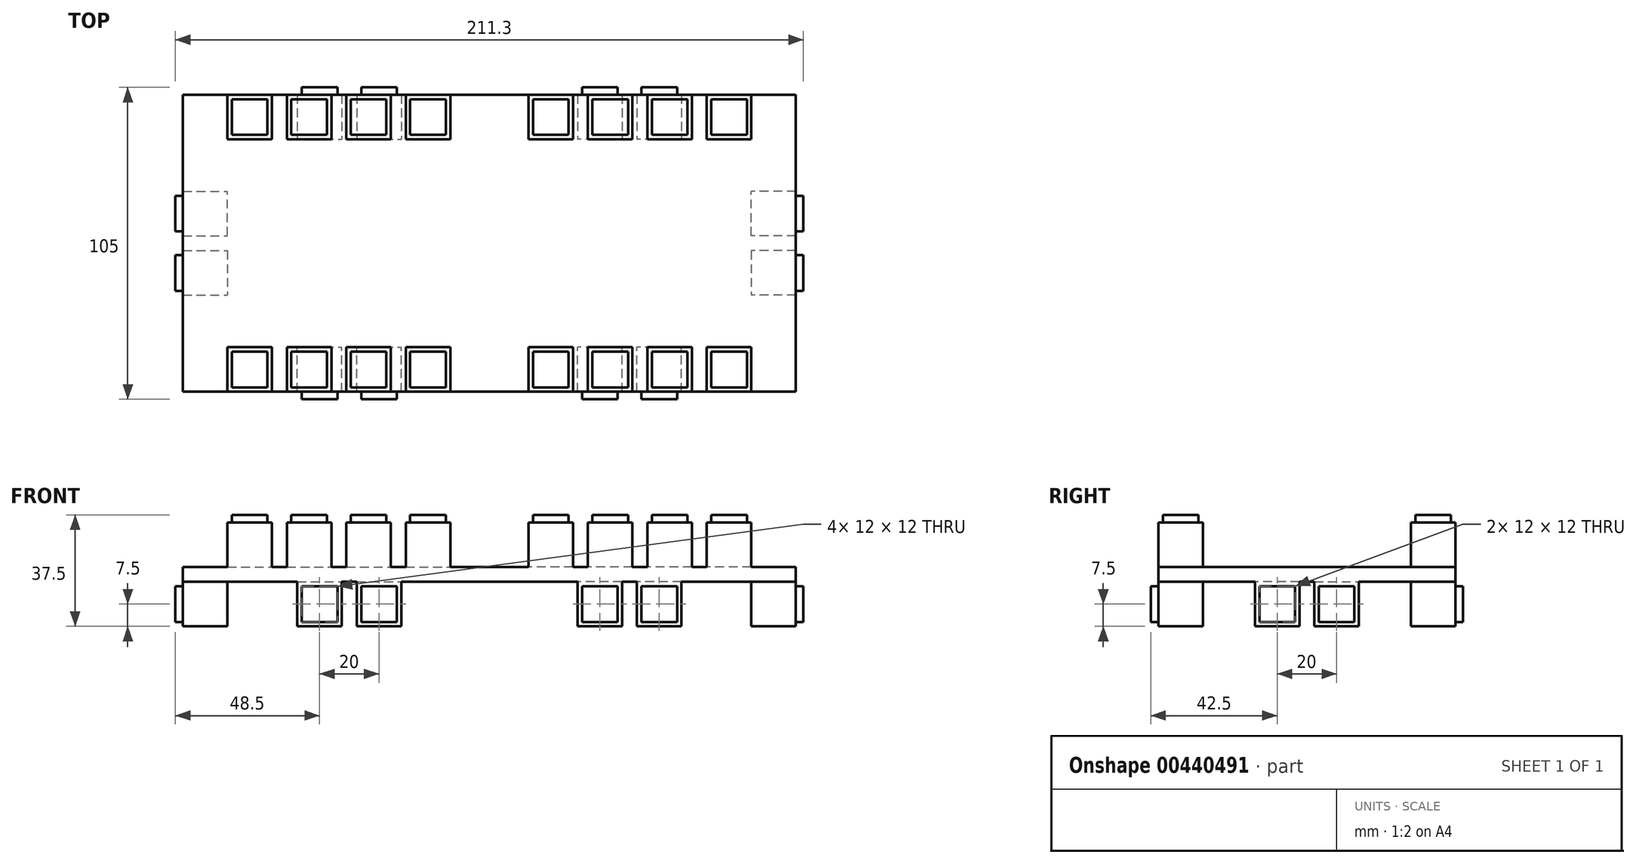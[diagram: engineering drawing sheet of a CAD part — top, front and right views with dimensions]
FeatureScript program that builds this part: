
annotation { "Feature Type Name" : "Feature", "Feature Type Description" : "" }
export const myFeature = defineFeature(function(context is Context, id is Id, definition is map)
    precondition{}
    {
        {
            var Q0;
            Q0=qCreatedBy(makeId("Top.planeOp"),FACE);
            var sketch = newSketch(context, id + "F0", { "sketchPlane" : qUnion([Q0])});
            skLineSegment(sketch, "E0.bottom", {"start": v(-103.15, 50) * mm, "end": v(103.15, 50) * mm});
            skLineSegment(sketch, "E0.top", {"start": v(-103.15, -50) * mm, "end": v(103.15, -50) * mm});
            skLineSegment(sketch, "E0.left", {"start": v(-103.15, 50) * mm, "end": v(-103.15, -50) * mm});
            skLineSegment(sketch, "E0.right", {"start": v(103.15, 50) * mm, "end": v(103.15, -50) * mm});
            skPoint(sketch, "E0.middle", {"position": v(0, 0) * mm});
            skSolve(sketch);
        }
        {
            var Q0;
            Q0 = qSketchRegion(id + "F0", true);
            extrude(context, id + "F1", {"entities" : qUnion([Q0]), "depth" : 5 * mm});
        }
        {
            var Q0;
            Q0=makeQuery(id+"F1.opExtrude","CAP_FACE",FACE,{"disambiguationData":[OSD([sQuery(id+"F0.wireOp",EDGE,"E0.bottom"),sQuery(id+"F0.wireOp",EDGE,"E0.top"),sQuery(id+"F0.wireOp",EDGE,"E0.left"),sQuery(id+"F0.wireOp",EDGE,"E0.right")])],"isStart":false});
            var sketch = newSketch(context, id + "F2", { "sketchPlane" : qUnion([Q0])});
            skLineSegment(sketch, "E1.bottom", {"start": v(-88.15, 50) * mm, "end": v(-73.15, 50) * mm});
            skLineSegment(sketch, "E1.top", {"start": v(-88.15, 35) * mm, "end": v(-73.15, 35) * mm});
            skLineSegment(sketch, "E1.left", {"start": v(-88.15, 50) * mm, "end": v(-88.15, 35) * mm});
            skLineSegment(sketch, "E1.right", {"start": v(-73.15, 50) * mm, "end": v(-73.15, 35) * mm});
            skLineSegment(sketch, "E2.bottom", {"start": v(-68.15, 50) * mm, "end": v(-53.15, 50) * mm});
            skLineSegment(sketch, "E2.top", {"start": v(-68.15, 35) * mm, "end": v(-53.15, 35) * mm});
            skLineSegment(sketch, "E2.left", {"start": v(-68.15, 50) * mm, "end": v(-68.15, 35) * mm});
            skLineSegment(sketch, "E2.right", {"start": v(-53.15, 50) * mm, "end": v(-53.15, 35) * mm});
            skLineSegment(sketch, "E3.bottom", {"start": v(-48.15, 50) * mm, "end": v(-33.15, 50) * mm});
            skLineSegment(sketch, "E3.top", {"start": v(-48.15, 35) * mm, "end": v(-33.15, 35) * mm});
            skLineSegment(sketch, "E3.left", {"start": v(-48.15, 50) * mm, "end": v(-48.15, 35) * mm});
            skLineSegment(sketch, "E3.right", {"start": v(-33.15, 50) * mm, "end": v(-33.15, 35) * mm});
            skLineSegment(sketch, "E4.bottom", {"start": v(-28.15, 50) * mm, "end": v(-13.15, 50) * mm});
            skLineSegment(sketch, "E4.top", {"start": v(-28.15, 35) * mm, "end": v(-13.15, 35) * mm});
            skLineSegment(sketch, "E4.left", {"start": v(-28.15, 50) * mm, "end": v(-28.15, 35) * mm});
            skLineSegment(sketch, "E4.right", {"start": v(-13.15, 50) * mm, "end": v(-13.15, 35) * mm});
            skLineSegment(sketch, "E5", {"start": v(0, 50) * mm, "end": v(0, -50) * mm, "construction": true});
            skLineSegment(sketch, "E6", {"start": v(-103.15, 0) * mm, "end": v(103.15, 0) * mm, "construction": true});
            skLineSegment(sketch, "E7.MirrorCS", {"start": v(-28.15, -35) * mm, "end": v(-13.15, -35) * mm});
            skLineSegment(sketch, "E8.MirrorCS", {"start": v(-13.15, -50) * mm, "end": v(-13.15, -35) * mm});
            skLineSegment(sketch, "E9.MirrorCS", {"start": v(-28.15, -50) * mm, "end": v(-13.15, -50) * mm});
            skLineSegment(sketch, "E10.MirrorCS", {"start": v(-28.15, -50) * mm, "end": v(-28.15, -35) * mm});
            skLineSegment(sketch, "E11.MirrorCS", {"start": v(-48.15, -35) * mm, "end": v(-33.15, -35) * mm});
            skLineSegment(sketch, "E12.MirrorCS", {"start": v(-33.15, -50) * mm, "end": v(-33.15, -35) * mm});
            skLineSegment(sketch, "E13.MirrorCS", {"start": v(-48.15, -50) * mm, "end": v(-33.15, -50) * mm});
            skLineSegment(sketch, "E14.MirrorCS", {"start": v(-48.15, -50) * mm, "end": v(-48.15, -35) * mm});
            skLineSegment(sketch, "E15.MirrorCS", {"start": v(-68.15, -35) * mm, "end": v(-53.15, -35) * mm});
            skLineSegment(sketch, "E16.MirrorCS", {"start": v(-53.15, -50) * mm, "end": v(-53.15, -35) * mm});
            skLineSegment(sketch, "E17.MirrorCS", {"start": v(-68.15, -50) * mm, "end": v(-53.15, -50) * mm});
            skLineSegment(sketch, "E18.MirrorCS", {"start": v(-68.15, -50) * mm, "end": v(-68.15, -35) * mm});
            skLineSegment(sketch, "E19.MirrorCS", {"start": v(-73.15, -50) * mm, "end": v(-73.15, -35) * mm});
            skLineSegment(sketch, "E20.MirrorCS", {"start": v(-88.15, -35) * mm, "end": v(-73.15, -35) * mm});
            skLineSegment(sketch, "E21.MirrorCS", {"start": v(-88.15, -50) * mm, "end": v(-73.15, -50) * mm});
            skLineSegment(sketch, "E22.MirrorCS", {"start": v(-88.15, -50) * mm, "end": v(-88.15, -35) * mm});
            skLineSegment(sketch, "E23.MirrorCS", {"start": v(28.15, -50) * mm, "end": v(13.15, -50) * mm});
            skLineSegment(sketch, "E24.MirrorCS", {"start": v(13.15, -50) * mm, "end": v(13.15, -35) * mm});
            skLineSegment(sketch, "E25.MirrorCS", {"start": v(28.15, -35) * mm, "end": v(13.15, -35) * mm});
            skLineSegment(sketch, "E26.MirrorCS", {"start": v(28.15, -50) * mm, "end": v(28.15, -35) * mm});
            skLineSegment(sketch, "E27.MirrorCS", {"start": v(48.15, -50) * mm, "end": v(33.15, -50) * mm});
            skLineSegment(sketch, "E28.MirrorCS", {"start": v(33.15, -50) * mm, "end": v(33.15, -35) * mm});
            skLineSegment(sketch, "E29.MirrorCS", {"start": v(48.15, -35) * mm, "end": v(33.15, -35) * mm});
            skLineSegment(sketch, "E30.MirrorCS", {"start": v(48.15, -50) * mm, "end": v(48.15, -35) * mm});
            skLineSegment(sketch, "E31.MirrorCS", {"start": v(53.15, -50) * mm, "end": v(53.15, -35) * mm});
            skLineSegment(sketch, "E32.MirrorCS", {"start": v(68.15, -50) * mm, "end": v(53.15, -50) * mm});
            skLineSegment(sketch, "E33.MirrorCS", {"start": v(68.15, -50) * mm, "end": v(68.15, -35) * mm});
            skLineSegment(sketch, "E34.MirrorCS", {"start": v(68.15, -35) * mm, "end": v(53.15, -35) * mm});
            skLineSegment(sketch, "E35.MirrorCS", {"start": v(88.15, -50) * mm, "end": v(73.15, -50) * mm});
            skLineSegment(sketch, "E36.MirrorCS", {"start": v(73.15, -50) * mm, "end": v(73.15, -35) * mm});
            skLineSegment(sketch, "E37.MirrorCS", {"start": v(88.15, -35) * mm, "end": v(73.15, -35) * mm});
            skLineSegment(sketch, "E38.MirrorCS", {"start": v(88.15, -50) * mm, "end": v(88.15, -35) * mm});
            skLineSegment(sketch, "E39.MirrorCS", {"start": v(28.15, 35) * mm, "end": v(13.15, 35) * mm});
            skLineSegment(sketch, "E40.MirrorCS", {"start": v(13.15, 50) * mm, "end": v(13.15, 35) * mm});
            skLineSegment(sketch, "E41.MirrorCS", {"start": v(28.15, 50) * mm, "end": v(13.15, 50) * mm});
            skLineSegment(sketch, "E42.MirrorCS", {"start": v(28.15, 50) * mm, "end": v(28.15, 35) * mm});
            skLineSegment(sketch, "E43.MirrorCS", {"start": v(48.15, 35) * mm, "end": v(33.15, 35) * mm});
            skLineSegment(sketch, "E44.MirrorCS", {"start": v(33.15, 50) * mm, "end": v(33.15, 35) * mm});
            skLineSegment(sketch, "E45.MirrorCS", {"start": v(48.15, 50) * mm, "end": v(33.15, 50) * mm});
            skLineSegment(sketch, "E46.MirrorCS", {"start": v(48.15, 50) * mm, "end": v(48.15, 35) * mm});
            skLineSegment(sketch, "E47.MirrorCS", {"start": v(68.15, 35) * mm, "end": v(53.15, 35) * mm});
            skLineSegment(sketch, "E48.MirrorCS", {"start": v(53.15, 50) * mm, "end": v(53.15, 35) * mm});
            skLineSegment(sketch, "E49.MirrorCS", {"start": v(68.15, 50) * mm, "end": v(53.15, 50) * mm});
            skLineSegment(sketch, "E50.MirrorCS", {"start": v(68.15, 50) * mm, "end": v(68.15, 35) * mm});
            skLineSegment(sketch, "E51.MirrorCS", {"start": v(88.15, 35) * mm, "end": v(73.15, 35) * mm});
            skLineSegment(sketch, "E52.MirrorCS", {"start": v(73.15, 50) * mm, "end": v(73.15, 35) * mm});
            skLineSegment(sketch, "E53.MirrorCS", {"start": v(88.15, 50) * mm, "end": v(88.15, 35) * mm});
            skLineSegment(sketch, "E54.MirrorCS", {"start": v(88.15, 50) * mm, "end": v(73.15, 50) * mm});
            skSolve(sketch);
        }
        {
            var Q0;
            Q0 = qSketchRegion(id + "F2", true);
            extrude(context, id + "F3", {"entities" : qUnion([Q0]), "operationType" : NewBodyOperationType.ADD, "depth" : 15 * mm});
        }
        {
            var Q0;
            Q0=makeQuery(id+"F1.opExtrude","CAP_FACE",FACE,{"disambiguationData":[OSD([sQuery(id+"F0.wireOp",EDGE,"E0.bottom"),sQuery(id+"F0.wireOp",EDGE,"E0.top"),sQuery(id+"F0.wireOp",EDGE,"E0.left"),sQuery(id+"F0.wireOp",EDGE,"E0.right")])],"isStart":true});
            var sketch = newSketch(context, id + "F4", { "sketchPlane" : qUnion([Q0])});
            skLineSegment(sketch, "E55.bottom", {"start": v(103.15, -2.5) * mm, "end": v(88.15, -2.5) * mm});
            skLineSegment(sketch, "E55.top", {"start": v(103.15, -17.5) * mm, "end": v(88.15, -17.5) * mm});
            skLineSegment(sketch, "E55.left", {"start": v(103.15, -2.5) * mm, "end": v(103.15, -17.5) * mm});
            skLineSegment(sketch, "E55.right", {"start": v(88.15, -2.5) * mm, "end": v(88.15, -17.5) * mm});
            skLineSegment(sketch, "E56", {"start": v(0, -50) * mm, "end": v(0, 50) * mm, "construction": true});
            skLineSegment(sketch, "E57", {"start": v(-103.15, 0) * mm, "end": v(103.15, 0) * mm, "construction": true});
            skLineSegment(sketch, "E58.bottom", {"start": v(103.15, 2.5) * mm, "end": v(88.15, 2.5) * mm});
            skLineSegment(sketch, "E58.top", {"start": v(103.15, 17.5) * mm, "end": v(88.15, 17.5) * mm});
            skLineSegment(sketch, "E58.left", {"start": v(103.15, 2.5) * mm, "end": v(103.15, 17.5) * mm});
            skLineSegment(sketch, "E58.right", {"start": v(88.15, 2.5) * mm, "end": v(88.15, 17.5) * mm});
            skLineSegment(sketch, "E59.bottom", {"start": v(64.65, 50) * mm, "end": v(49.65, 50) * mm});
            skLineSegment(sketch, "E59.top", {"start": v(64.65, 35) * mm, "end": v(49.65, 35) * mm});
            skLineSegment(sketch, "E59.left", {"start": v(64.65, 50) * mm, "end": v(64.65, 35) * mm});
            skLineSegment(sketch, "E59.right", {"start": v(49.65, 50) * mm, "end": v(49.65, 35) * mm});
            skLineSegment(sketch, "E60.bottom", {"start": v(44.65, 50) * mm, "end": v(29.65, 50) * mm});
            skLineSegment(sketch, "E60.top", {"start": v(44.65, 35) * mm, "end": v(29.65, 35) * mm});
            skLineSegment(sketch, "E60.left", {"start": v(44.65, 50) * mm, "end": v(44.65, 35) * mm});
            skLineSegment(sketch, "E60.right", {"start": v(29.65, 50) * mm, "end": v(29.65, 35) * mm});
            skLineSegment(sketch, "E61.bottom", {"start": v(64.65, -50) * mm, "end": v(49.65, -50) * mm});
            skLineSegment(sketch, "E61.top", {"start": v(64.65, -35) * mm, "end": v(49.65, -35) * mm});
            skLineSegment(sketch, "E61.left", {"start": v(64.65, -50) * mm, "end": v(64.65, -35) * mm});
            skLineSegment(sketch, "E61.right", {"start": v(49.65, -50) * mm, "end": v(49.65, -35) * mm});
            skLineSegment(sketch, "E62.bottom", {"start": v(44.65, -50) * mm, "end": v(29.65, -50) * mm});
            skLineSegment(sketch, "E62.top", {"start": v(44.65, -35) * mm, "end": v(29.65, -35) * mm});
            skLineSegment(sketch, "E62.left", {"start": v(44.65, -50) * mm, "end": v(44.65, -35) * mm});
            skLineSegment(sketch, "E62.right", {"start": v(29.65, -50) * mm, "end": v(29.65, -35) * mm});
            skLineSegment(sketch, "E63.MirrorCS", {"start": v(-103.15, 2.5) * mm, "end": v(-103.15, 17.5) * mm});
            skLineSegment(sketch, "E64.MirrorCS", {"start": v(-103.15, 17.5) * mm, "end": v(-88.15, 17.5) * mm});
            skLineSegment(sketch, "E65.MirrorCS", {"start": v(-88.15, 2.5) * mm, "end": v(-88.15, 17.5) * mm});
            skLineSegment(sketch, "E66.MirrorCS", {"start": v(-103.15, 2.5) * mm, "end": v(-88.15, 2.5) * mm});
            skLineSegment(sketch, "E67.MirrorCS", {"start": v(-103.15, -2.5) * mm, "end": v(-103.15, -17.5) * mm});
            skLineSegment(sketch, "E68.MirrorCS", {"start": v(-103.15, -2.5) * mm, "end": v(-88.15, -2.5) * mm});
            skLineSegment(sketch, "E69.MirrorCS", {"start": v(-88.15, -2.5) * mm, "end": v(-88.15, -17.5) * mm});
            skLineSegment(sketch, "E70.MirrorCS", {"start": v(-103.15, -17.5) * mm, "end": v(-88.15, -17.5) * mm});
            skLineSegment(sketch, "E71.MirrorCS", {"start": v(-64.65, 50) * mm, "end": v(-49.65, 50) * mm});
            skLineSegment(sketch, "E72.MirrorCS", {"start": v(-64.65, 50) * mm, "end": v(-64.65, 35) * mm});
            skLineSegment(sketch, "E73.MirrorCS", {"start": v(-49.65, 50) * mm, "end": v(-49.65, 35) * mm});
            skLineSegment(sketch, "E74.MirrorCS", {"start": v(-64.65, 35) * mm, "end": v(-49.65, 35) * mm});
            skLineSegment(sketch, "E75.MirrorCS", {"start": v(-64.65, -35) * mm, "end": v(-49.65, -35) * mm});
            skLineSegment(sketch, "E76.MirrorCS", {"start": v(-64.65, -50) * mm, "end": v(-64.65, -35) * mm});
            skLineSegment(sketch, "E77.MirrorCS", {"start": v(-64.65, -50) * mm, "end": v(-49.65, -50) * mm});
            skLineSegment(sketch, "E78.MirrorCS", {"start": v(-49.65, -50) * mm, "end": v(-49.65, -35) * mm});
            skLineSegment(sketch, "E79.MirrorCS", {"start": v(-44.65, 50) * mm, "end": v(-29.65, 50) * mm});
            skLineSegment(sketch, "E80.MirrorCS", {"start": v(-44.65, 50) * mm, "end": v(-44.65, 35) * mm});
            skLineSegment(sketch, "E81.MirrorCS", {"start": v(-44.65, -50) * mm, "end": v(-44.65, -35) * mm});
            skLineSegment(sketch, "E82.MirrorCS", {"start": v(-44.65, -50) * mm, "end": v(-29.65, -50) * mm});
            skLineSegment(sketch, "E83.MirrorCS", {"start": v(-44.65, 35) * mm, "end": v(-29.65, 35) * mm});
            skLineSegment(sketch, "E84.MirrorCS", {"start": v(-44.65, -35) * mm, "end": v(-29.65, -35) * mm});
            skLineSegment(sketch, "E85.MirrorCS", {"start": v(-29.65, -50) * mm, "end": v(-29.65, -35) * mm});
            skLineSegment(sketch, "E86.MirrorCS", {"start": v(-29.65, 50) * mm, "end": v(-29.65, 35) * mm});
            skSolve(sketch);
        }
        {
            var Q0;
            Q0 = qSketchRegion(id + "F4", true);
            extrude(context, id + "F5", {"entities" : qUnion([Q0]), "operationType" : NewBodyOperationType.ADD, "depth" : 15 * mm});
        }
        {
            var Q0;
            Q0=makeQuery(id+"F3.opExtrude","CAP_FACE",FACE,{"disambiguationData":[OSD([sQuery(id+"F2.wireOp",EDGE,"E1.bottom"),sQuery(id+"F2.wireOp",EDGE,"E1.top"),sQuery(id+"F2.wireOp",EDGE,"E1.left"),sQuery(id+"F2.wireOp",EDGE,"E1.right")])],"isStart":false});
            var sketch = newSketch(context, id + "F6", { "sketchPlane" : qUnion([Q0])});
            skLineSegment(sketch, "E87.bottom", {"start": v(-86.65, 48.5) * mm, "end": v(-74.65, 48.5) * mm});
            skLineSegment(sketch, "E87.top", {"start": v(-86.65, 36.5) * mm, "end": v(-74.65, 36.5) * mm});
            skLineSegment(sketch, "E87.left", {"start": v(-86.65, 48.5) * mm, "end": v(-86.65, 36.5) * mm});
            skLineSegment(sketch, "E87.right", {"start": v(-74.65, 48.5) * mm, "end": v(-74.65, 36.5) * mm});
            skLineSegment(sketch, "E88.1.0.0", {"start": v(-66.65, 48.5) * mm, "end": v(-54.65, 48.5) * mm});
            skLineSegment(sketch, "E88.1.0.1", {"start": v(-66.65, 48.5) * mm, "end": v(-66.65, 36.5) * mm});
            skLineSegment(sketch, "E88.1.0.2", {"start": v(-66.65, 36.5) * mm, "end": v(-54.65, 36.5) * mm});
            skLineSegment(sketch, "E88.1.0.3", {"start": v(-54.65, 48.5) * mm, "end": v(-54.65, 36.5) * mm});
            skLineSegment(sketch, "E88.2.0.0", {"start": v(-46.65, 48.5) * mm, "end": v(-34.65, 48.5) * mm});
            skLineSegment(sketch, "E88.2.0.1", {"start": v(-46.65, 48.5) * mm, "end": v(-46.65, 36.5) * mm});
            skLineSegment(sketch, "E88.2.0.2", {"start": v(-46.65, 36.5) * mm, "end": v(-34.65, 36.5) * mm});
            skLineSegment(sketch, "E88.2.0.3", {"start": v(-34.65, 48.5) * mm, "end": v(-34.65, 36.5) * mm});
            skLineSegment(sketch, "E88.3.0.0", {"start": v(-26.65, 48.5) * mm, "end": v(-14.65, 48.5) * mm});
            skLineSegment(sketch, "E88.3.0.1", {"start": v(-26.65, 48.5) * mm, "end": v(-26.65, 36.5) * mm});
            skLineSegment(sketch, "E88.3.0.2", {"start": v(-26.65, 36.5) * mm, "end": v(-14.65, 36.5) * mm});
            skLineSegment(sketch, "E88.3.0.3", {"start": v(-14.65, 48.5) * mm, "end": v(-14.65, 36.5) * mm});
            skLineSegment(sketch, "E88.direction1", {"start": v(-86.65, 36.5) * mm, "end": v(-66.65, 36.5) * mm, "construction": true});
            skLineSegment(sketch, "E89.bottom", {"start": v(14.65, 48.5) * mm, "end": v(26.65, 48.5) * mm});
            skLineSegment(sketch, "E89.top", {"start": v(14.65, 36.5) * mm, "end": v(26.65, 36.5) * mm});
            skLineSegment(sketch, "E89.left", {"start": v(14.65, 48.5) * mm, "end": v(14.65, 36.5) * mm});
            skLineSegment(sketch, "E89.right", {"start": v(26.65, 48.5) * mm, "end": v(26.65, 36.5) * mm});
            skLineSegment(sketch, "E90.1.0.0", {"start": v(34.65, 48.5) * mm, "end": v(46.65, 48.5) * mm});
            skLineSegment(sketch, "E90.1.0.1", {"start": v(34.65, 48.5) * mm, "end": v(34.65, 36.5) * mm});
            skLineSegment(sketch, "E90.1.0.2", {"start": v(34.65, 36.5) * mm, "end": v(46.65, 36.5) * mm});
            skLineSegment(sketch, "E90.1.0.3", {"start": v(46.65, 48.5) * mm, "end": v(46.65, 36.5) * mm});
            skLineSegment(sketch, "E90.2.0.0", {"start": v(54.65, 48.5) * mm, "end": v(66.65, 48.5) * mm});
            skLineSegment(sketch, "E90.2.0.1", {"start": v(54.65, 48.5) * mm, "end": v(54.65, 36.5) * mm});
            skLineSegment(sketch, "E90.2.0.2", {"start": v(54.65, 36.5) * mm, "end": v(66.65, 36.5) * mm});
            skLineSegment(sketch, "E90.2.0.3", {"start": v(66.65, 48.5) * mm, "end": v(66.65, 36.5) * mm});
            skLineSegment(sketch, "E90.3.0.0", {"start": v(74.65, 48.5) * mm, "end": v(86.65, 48.5) * mm});
            skLineSegment(sketch, "E90.3.0.1", {"start": v(74.65, 48.5) * mm, "end": v(74.65, 36.5) * mm});
            skLineSegment(sketch, "E90.3.0.2", {"start": v(74.65, 36.5) * mm, "end": v(86.65, 36.5) * mm});
            skLineSegment(sketch, "E90.3.0.3", {"start": v(86.65, 48.5) * mm, "end": v(86.65, 36.5) * mm});
            skLineSegment(sketch, "E90.direction1", {"start": v(14.65, 36.5) * mm, "end": v(34.65, 36.5) * mm, "construction": true});
            skLineSegment(sketch, "E91.bottom", {"start": v(74.65, -36.5) * mm, "end": v(86.65, -36.5) * mm});
            skLineSegment(sketch, "E91.top", {"start": v(74.65, -48.5) * mm, "end": v(86.65, -48.5) * mm});
            skLineSegment(sketch, "E91.left", {"start": v(74.65, -36.5) * mm, "end": v(74.65, -48.5) * mm});
            skLineSegment(sketch, "E91.right", {"start": v(86.65, -36.5) * mm, "end": v(86.65, -48.5) * mm});
            skLineSegment(sketch, "E92.1.0.0", {"start": v(54.65, -36.5) * mm, "end": v(66.65, -36.5) * mm});
            skLineSegment(sketch, "E92.1.0.1", {"start": v(54.65, -36.5) * mm, "end": v(54.65, -48.5) * mm});
            skLineSegment(sketch, "E92.1.0.2", {"start": v(54.65, -48.5) * mm, "end": v(66.65, -48.5) * mm});
            skLineSegment(sketch, "E92.1.0.3", {"start": v(66.65, -36.5) * mm, "end": v(66.65, -48.5) * mm});
            skLineSegment(sketch, "E92.2.0.0", {"start": v(34.65, -36.5) * mm, "end": v(46.65, -36.5) * mm});
            skLineSegment(sketch, "E92.2.0.1", {"start": v(34.65, -36.5) * mm, "end": v(34.65, -48.5) * mm});
            skLineSegment(sketch, "E92.2.0.2", {"start": v(34.65, -48.5) * mm, "end": v(46.65, -48.5) * mm});
            skLineSegment(sketch, "E92.2.0.3", {"start": v(46.65, -36.5) * mm, "end": v(46.65, -48.5) * mm});
            skLineSegment(sketch, "E92.3.0.0", {"start": v(14.65, -36.5) * mm, "end": v(26.65, -36.5) * mm});
            skLineSegment(sketch, "E92.3.0.1", {"start": v(14.65, -36.5) * mm, "end": v(14.65, -48.5) * mm});
            skLineSegment(sketch, "E92.3.0.2", {"start": v(14.65, -48.5) * mm, "end": v(26.65, -48.5) * mm});
            skLineSegment(sketch, "E92.3.0.3", {"start": v(26.65, -36.5) * mm, "end": v(26.65, -48.5) * mm});
            skLineSegment(sketch, "E92.direction1", {"start": v(74.65, -48.5) * mm, "end": v(54.65, -48.5) * mm, "construction": true});
            skLineSegment(sketch, "E93.bottom", {"start": v(-86.65, -36.5) * mm, "end": v(-74.65, -36.5) * mm});
            skLineSegment(sketch, "E93.top", {"start": v(-86.65, -48.5) * mm, "end": v(-74.65, -48.5) * mm});
            skLineSegment(sketch, "E93.left", {"start": v(-86.65, -36.5) * mm, "end": v(-86.65, -48.5) * mm});
            skLineSegment(sketch, "E93.right", {"start": v(-74.65, -36.5) * mm, "end": v(-74.65, -48.5) * mm});
            skLineSegment(sketch, "E94.1.0.0", {"start": v(-66.65, -36.5) * mm, "end": v(-54.65, -36.5) * mm});
            skLineSegment(sketch, "E94.1.0.1", {"start": v(-66.65, -36.5) * mm, "end": v(-66.65, -48.5) * mm});
            skLineSegment(sketch, "E94.1.0.2", {"start": v(-66.65, -48.5) * mm, "end": v(-54.65, -48.5) * mm});
            skLineSegment(sketch, "E94.1.0.3", {"start": v(-54.65, -36.5) * mm, "end": v(-54.65, -48.5) * mm});
            skLineSegment(sketch, "E94.2.0.0", {"start": v(-46.65, -36.5) * mm, "end": v(-34.65, -36.5) * mm});
            skLineSegment(sketch, "E94.2.0.1", {"start": v(-46.65, -36.5) * mm, "end": v(-46.65, -48.5) * mm});
            skLineSegment(sketch, "E94.2.0.2", {"start": v(-46.65, -48.5) * mm, "end": v(-34.65, -48.5) * mm});
            skLineSegment(sketch, "E94.2.0.3", {"start": v(-34.65, -36.5) * mm, "end": v(-34.65, -48.5) * mm});
            skLineSegment(sketch, "E94.3.0.0", {"start": v(-26.65, -36.5) * mm, "end": v(-14.65, -36.5) * mm});
            skLineSegment(sketch, "E94.3.0.1", {"start": v(-26.65, -36.5) * mm, "end": v(-26.65, -48.5) * mm});
            skLineSegment(sketch, "E94.3.0.2", {"start": v(-26.65, -48.5) * mm, "end": v(-14.65, -48.5) * mm});
            skLineSegment(sketch, "E94.3.0.3", {"start": v(-14.65, -36.5) * mm, "end": v(-14.65, -48.5) * mm});
            skLineSegment(sketch, "E94.direction1", {"start": v(-86.65, -48.5) * mm, "end": v(-66.65, -48.5) * mm, "construction": true});
            skSolve(sketch);
        }
        {
            var Q0;
            Q0 = qSketchRegion(id + "F6", true);
            extrude(context, id + "F7", {"entities" : qUnion([Q0]), "operationType" : NewBodyOperationType.ADD, "depth" : 2.5 * mm});
        }
        {
            var Q0;
            Q0=makeQuery(id+"F5.boolean.opBoolean","MERGE",FACE,{"derivedFrom":[makeQuery(id+"F1.opExtrude","SWEPT_FACE",FACE,{"disambiguationData":[OSD([sQuery(id+"F0.wireOp",EDGE,"E0.right")])]}),makeQuery(id+"F5.opExtrude","SWEPT_FACE",FACE,{"disambiguationData":[OSD([sQuery(id+"F4.wireOp",EDGE,"E55.left")])]}),makeQuery(id+"F5.opExtrude","SWEPT_FACE",FACE,{"disambiguationData":[OSD([sQuery(id+"F4.wireOp",EDGE,"E58.left")])]})]});
            var sketch = newSketch(context, id + "F8", { "sketchPlane" : qUnion([Q0])});
            skLineSegment(sketch, "E95.bottom", {"start": v(-16, -1.5) * mm, "end": v(-4, -1.5) * mm});
            skLineSegment(sketch, "E95.top", {"start": v(-16, -13.5) * mm, "end": v(-4, -13.5) * mm});
            skLineSegment(sketch, "E95.left", {"start": v(-16, -1.5) * mm, "end": v(-16, -13.5) * mm});
            skLineSegment(sketch, "E95.right", {"start": v(-4, -1.5) * mm, "end": v(-4, -13.5) * mm});
            skLineSegment(sketch, "E96.1.0.0", {"start": v(4, -1.5) * mm, "end": v(16, -1.5) * mm});
            skLineSegment(sketch, "E96.1.0.1", {"start": v(4, -1.5) * mm, "end": v(4, -13.5) * mm});
            skLineSegment(sketch, "E96.1.0.2", {"start": v(4, -13.5) * mm, "end": v(16, -13.5) * mm});
            skLineSegment(sketch, "E96.1.0.3", {"start": v(16, -1.5) * mm, "end": v(16, -13.5) * mm});
            skLineSegment(sketch, "E96.direction1", {"start": v(-16, -13.5) * mm, "end": v(4, -13.5) * mm, "construction": true});
            skSolve(sketch);
        }
        {
            var Q0;
            Q0 = qSketchRegion(id + "F8", true);
            extrude(context, id + "F9", {"entities" : qUnion([Q0]), "operationType" : NewBodyOperationType.ADD, "depth" : 2.5 * mm});
        }
        {
            var Q0;
            Q0=makeQuery(id+"F5.boolean.opBoolean","MERGE",FACE,{"derivedFrom":[makeQuery(id+"F1.opExtrude","SWEPT_FACE",FACE,{"disambiguationData":[OSD([sQuery(id+"F0.wireOp",EDGE,"E0.left")])]}),makeQuery(id+"F5.opExtrude","SWEPT_FACE",FACE,{"disambiguationData":[OSD([sQuery(id+"F4.wireOp",EDGE,"E63.MirrorCS")])]}),makeQuery(id+"F5.opExtrude","SWEPT_FACE",FACE,{"disambiguationData":[OSD([sQuery(id+"F4.wireOp",EDGE,"E67.MirrorCS")])]})]});
            var sketch = newSketch(context, id + "F10", { "sketchPlane" : qUnion([Q0])});
            skLineSegment(sketch, "E97.bottom", {"start": v(-4, -13.5) * mm, "end": v(-16, -13.5) * mm});
            skLineSegment(sketch, "E97.top", {"start": v(-4, -1.5) * mm, "end": v(-16, -1.5) * mm});
            skLineSegment(sketch, "E97.left", {"start": v(-4, -13.5) * mm, "end": v(-4, -1.5) * mm});
            skLineSegment(sketch, "E97.right", {"start": v(-16, -13.5) * mm, "end": v(-16, -1.5) * mm});
            skLineSegment(sketch, "E98.1.0.0", {"start": v(16, -1.5) * mm, "end": v(4, -1.5) * mm});
            skLineSegment(sketch, "E98.1.0.1", {"start": v(4, -13.5) * mm, "end": v(4, -1.5) * mm});
            skLineSegment(sketch, "E98.1.0.2", {"start": v(16, -13.5) * mm, "end": v(4, -13.5) * mm});
            skLineSegment(sketch, "E98.1.0.3", {"start": v(16, -13.5) * mm, "end": v(16, -1.5) * mm});
            skLineSegment(sketch, "E98.direction1", {"start": v(-16, -13.5) * mm, "end": v(4, -13.5) * mm, "construction": true});
            skSolve(sketch);
        }
        {
            var Q0;
            Q0 = qSketchRegion(id + "F10", true);
            extrude(context, id + "F11", {"entities" : qUnion([Q0]), "operationType" : NewBodyOperationType.ADD, "depth" : 2.5 * mm});
        }
        {
            var Q0;
            Q0=makeQuery(id+"F5.boolean.opBoolean","MERGE",FACE,{"derivedFrom":[makeQuery(id+"F3.boolean.opBoolean","MERGE",FACE,{"derivedFrom":[makeQuery(id+"F1.opExtrude","SWEPT_FACE",FACE,{"disambiguationData":[OSD([sQuery(id+"F0.wireOp",EDGE,"E0.bottom")])]}),makeQuery(id+"F3.opExtrude","SWEPT_FACE",FACE,{"disambiguationData":[OSD([sQuery(id+"F2.wireOp",EDGE,"E1.bottom")])]}),makeQuery(id+"F3.opExtrude","SWEPT_FACE",FACE,{"disambiguationData":[OSD([sQuery(id+"F2.wireOp",EDGE,"E2.bottom")])]}),makeQuery(id+"F3.opExtrude","SWEPT_FACE",FACE,{"disambiguationData":[OSD([sQuery(id+"F2.wireOp",EDGE,"E3.bottom")])]}),makeQuery(id+"F3.opExtrude","SWEPT_FACE",FACE,{"disambiguationData":[OSD([sQuery(id+"F2.wireOp",EDGE,"E4.bottom")])]}),makeQuery(id+"F3.opExtrude","SWEPT_FACE",FACE,{"disambiguationData":[OSD([sQuery(id+"F2.wireOp",EDGE,"E41.MirrorCS")])]}),makeQuery(id+"F3.opExtrude","SWEPT_FACE",FACE,{"disambiguationData":[OSD([sQuery(id+"F2.wireOp",EDGE,"E45.MirrorCS")])]}),makeQuery(id+"F3.opExtrude","SWEPT_FACE",FACE,{"disambiguationData":[OSD([sQuery(id+"F2.wireOp",EDGE,"E49.MirrorCS")])]}),makeQuery(id+"F3.opExtrude","SWEPT_FACE",FACE,{"disambiguationData":[OSD([sQuery(id+"F2.wireOp",EDGE,"E54.MirrorCS")])]})]}),makeQuery(id+"F5.opExtrude","SWEPT_FACE",FACE,{"disambiguationData":[OSD([sQuery(id+"F4.wireOp",EDGE,"E61.bottom")])]}),makeQuery(id+"F5.opExtrude","SWEPT_FACE",FACE,{"disambiguationData":[OSD([sQuery(id+"F4.wireOp",EDGE,"E62.bottom")])]}),makeQuery(id+"F5.opExtrude","SWEPT_FACE",FACE,{"disambiguationData":[OSD([sQuery(id+"F4.wireOp",EDGE,"E77.MirrorCS")])]}),makeQuery(id+"F5.opExtrude","SWEPT_FACE",FACE,{"disambiguationData":[OSD([sQuery(id+"F4.wireOp",EDGE,"E82.MirrorCS")])]})]});
            var sketch = newSketch(context, id + "F12", { "sketchPlane" : qUnion([Q0])});
            skLineSegment(sketch, "E99.bottom", {"start": v(-43.15, -1.5) * mm, "end": v(-31.15, -1.5) * mm});
            skLineSegment(sketch, "E99.top", {"start": v(-43.15, -13.5) * mm, "end": v(-31.15, -13.5) * mm});
            skLineSegment(sketch, "E99.left", {"start": v(-43.15, -1.5) * mm, "end": v(-43.15, -13.5) * mm});
            skLineSegment(sketch, "E99.right", {"start": v(-31.15, -1.5) * mm, "end": v(-31.15, -13.5) * mm});
            skLineSegment(sketch, "E100.bottom", {"start": v(-63.15, -1.5) * mm, "end": v(-51.15, -1.5) * mm});
            skLineSegment(sketch, "E100.top", {"start": v(-63.15, -13.5) * mm, "end": v(-51.15, -13.5) * mm});
            skLineSegment(sketch, "E100.left", {"start": v(-63.15, -1.5) * mm, "end": v(-63.15, -13.5) * mm});
            skLineSegment(sketch, "E100.right", {"start": v(-51.15, -1.5) * mm, "end": v(-51.15, -13.5) * mm});
            skLineSegment(sketch, "E101.bottom", {"start": v(31.15, -1.5) * mm, "end": v(43.15, -1.5) * mm});
            skLineSegment(sketch, "E101.top", {"start": v(31.15, -13.5) * mm, "end": v(43.15, -13.5) * mm});
            skLineSegment(sketch, "E101.left", {"start": v(31.15, -1.5) * mm, "end": v(31.15, -13.5) * mm});
            skLineSegment(sketch, "E101.right", {"start": v(43.15, -1.5) * mm, "end": v(43.15, -13.5) * mm});
            skLineSegment(sketch, "E102.bottom", {"start": v(51.15, -1.5) * mm, "end": v(63.15, -1.5) * mm});
            skLineSegment(sketch, "E102.top", {"start": v(51.15, -13.5) * mm, "end": v(63.15, -13.5) * mm});
            skLineSegment(sketch, "E102.left", {"start": v(51.15, -1.5) * mm, "end": v(51.15, -13.5) * mm});
            skLineSegment(sketch, "E102.right", {"start": v(63.15, -1.5) * mm, "end": v(63.15, -13.5) * mm});
            skSolve(sketch);
        }
        {
            var Q0;
            Q0 = qSketchRegion(id + "F12", true);
            extrude(context, id + "F13", {"entities" : qUnion([Q0]), "operationType" : NewBodyOperationType.ADD, "depth" : 2.5 * mm});
        }
        {
            var Q0;
            Q0=makeQuery(id+"F5.boolean.opBoolean","MERGE",FACE,{"derivedFrom":[makeQuery(id+"F3.boolean.opBoolean","MERGE",FACE,{"derivedFrom":[makeQuery(id+"F1.opExtrude","SWEPT_FACE",FACE,{"disambiguationData":[OSD([sQuery(id+"F0.wireOp",EDGE,"E0.top")])]}),makeQuery(id+"F3.opExtrude","SWEPT_FACE",FACE,{"disambiguationData":[OSD([sQuery(id+"F2.wireOp",EDGE,"E9.MirrorCS")])]}),makeQuery(id+"F3.opExtrude","SWEPT_FACE",FACE,{"disambiguationData":[OSD([sQuery(id+"F2.wireOp",EDGE,"E13.MirrorCS")])]}),makeQuery(id+"F3.opExtrude","SWEPT_FACE",FACE,{"disambiguationData":[OSD([sQuery(id+"F2.wireOp",EDGE,"E17.MirrorCS")])]}),makeQuery(id+"F3.opExtrude","SWEPT_FACE",FACE,{"disambiguationData":[OSD([sQuery(id+"F2.wireOp",EDGE,"E21.MirrorCS")])]}),makeQuery(id+"F3.opExtrude","SWEPT_FACE",FACE,{"disambiguationData":[OSD([sQuery(id+"F2.wireOp",EDGE,"E23.MirrorCS")])]}),makeQuery(id+"F3.opExtrude","SWEPT_FACE",FACE,{"disambiguationData":[OSD([sQuery(id+"F2.wireOp",EDGE,"E27.MirrorCS")])]}),makeQuery(id+"F3.opExtrude","SWEPT_FACE",FACE,{"disambiguationData":[OSD([sQuery(id+"F2.wireOp",EDGE,"E32.MirrorCS")])]}),makeQuery(id+"F3.opExtrude","SWEPT_FACE",FACE,{"disambiguationData":[OSD([sQuery(id+"F2.wireOp",EDGE,"E35.MirrorCS")])]})]}),makeQuery(id+"F5.opExtrude","SWEPT_FACE",FACE,{"disambiguationData":[OSD([sQuery(id+"F4.wireOp",EDGE,"E59.bottom")])]}),makeQuery(id+"F5.opExtrude","SWEPT_FACE",FACE,{"disambiguationData":[OSD([sQuery(id+"F4.wireOp",EDGE,"E60.bottom")])]}),makeQuery(id+"F5.opExtrude","SWEPT_FACE",FACE,{"disambiguationData":[OSD([sQuery(id+"F4.wireOp",EDGE,"E71.MirrorCS")])]}),makeQuery(id+"F5.opExtrude","SWEPT_FACE",FACE,{"disambiguationData":[OSD([sQuery(id+"F4.wireOp",EDGE,"E79.MirrorCS")])]})]});
            var sketch = newSketch(context, id + "F14", { "sketchPlane" : qUnion([Q0])});
            skLineSegment(sketch, "E103.bottom", {"start": v(-51.15, -1.5) * mm, "end": v(-63.15, -1.5) * mm});
            skLineSegment(sketch, "E103.top", {"start": v(-51.15, -13.5) * mm, "end": v(-63.15, -13.5) * mm});
            skLineSegment(sketch, "E103.left", {"start": v(-51.15, -1.5) * mm, "end": v(-51.15, -13.5) * mm});
            skLineSegment(sketch, "E103.right", {"start": v(-63.15, -1.5) * mm, "end": v(-63.15, -13.5) * mm});
            skLineSegment(sketch, "E104.bottom", {"start": v(-31.15, -1.5) * mm, "end": v(-43.15, -1.5) * mm});
            skLineSegment(sketch, "E104.top", {"start": v(-31.15, -13.5) * mm, "end": v(-43.15, -13.5) * mm});
            skLineSegment(sketch, "E104.left", {"start": v(-31.15, -1.5) * mm, "end": v(-31.15, -13.5) * mm});
            skLineSegment(sketch, "E104.right", {"start": v(-43.15, -1.5) * mm, "end": v(-43.15, -13.5) * mm});
            skPoint(sketch, "E105.oppositeSnap0", {"position": v(-37.15, -13.5) * mm});
            skLineSegment(sketch, "E105.bottom", {"start": v(43.15, -1.5) * mm, "end": v(31.15, -1.5) * mm});
            skLineSegment(sketch, "E105.top", {"start": v(43.15, -13.5) * mm, "end": v(31.15, -13.5) * mm});
            skLineSegment(sketch, "E105.left", {"start": v(43.15, -1.5) * mm, "end": v(43.15, -13.5) * mm});
            skLineSegment(sketch, "E105.right", {"start": v(31.15, -1.5) * mm, "end": v(31.15, -13.5) * mm});
            skLineSegment(sketch, "E106.bottom", {"start": v(63.15, -1.5) * mm, "end": v(51.15, -1.5) * mm});
            skLineSegment(sketch, "E106.top", {"start": v(63.15, -13.5) * mm, "end": v(51.15, -13.5) * mm});
            skLineSegment(sketch, "E106.left", {"start": v(63.15, -1.5) * mm, "end": v(63.15, -13.5) * mm});
            skLineSegment(sketch, "E106.right", {"start": v(51.15, -1.5) * mm, "end": v(51.15, -13.5) * mm});
            skSolve(sketch);
        }
        {
            var Q0;
            Q0 = qSketchRegion(id + "F14", true);
            extrude(context, id + "F15", {"entities" : qUnion([Q0]), "operationType" : NewBodyOperationType.ADD, "depth" : 2.5 * mm});
        }
    });
